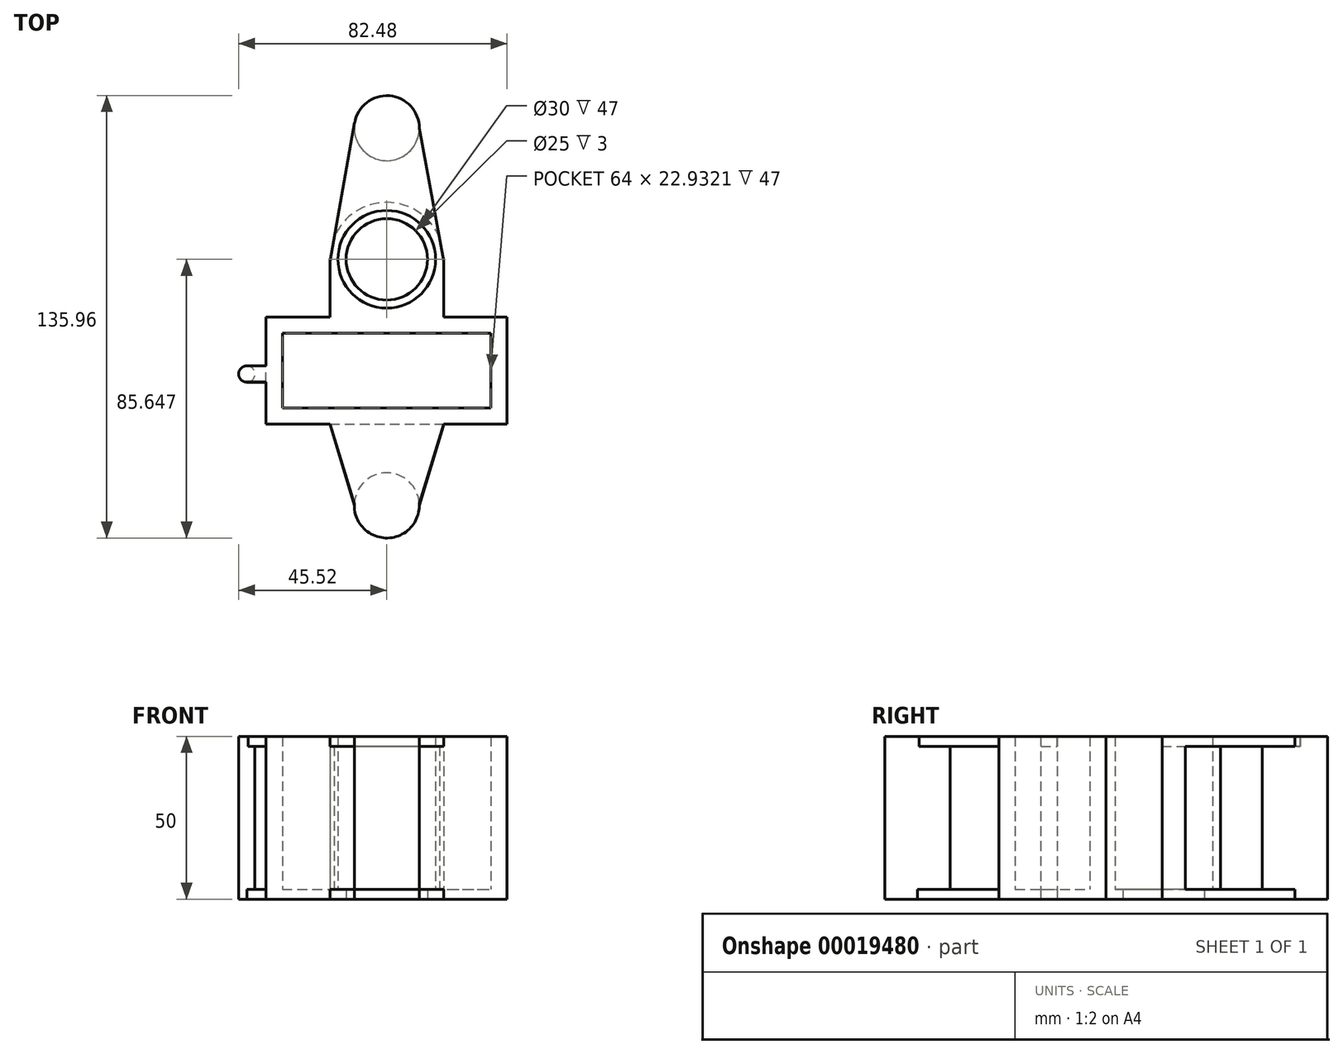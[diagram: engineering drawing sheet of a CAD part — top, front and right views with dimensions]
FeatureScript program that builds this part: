
annotation { "Feature Type Name" : "Feature", "Feature Type Description" : "" }
export const myFeature = defineFeature(function(context is Context, id is Id, definition is map)
    precondition{}
    {
        {
            var Q0;
            Q0=qCreatedBy(makeId("Top.planeOp"),FACE);
            var sketch = newSketch(context, id + "F0", { "sketchPlane" : qUnion([Q0])});
            skLineSegment(sketch, "E0.bottom", {"start": v(0, 0) * mm, "end": v(64, 0) * mm});
            skLineSegment(sketch, "E0.top", {"start": v(0, 22.93) * mm, "end": v(64, 22.93) * mm});
            skLineSegment(sketch, "E0.left", {"start": v(0, 0) * mm, "end": v(0, 22.93) * mm});
            skLineSegment(sketch, "E0.right", {"start": v(64, 0) * mm, "end": v(64, 22.93) * mm});
            skLineSegment(sketch, "E1.0", {"start": v(-5, 27.94) * mm, "end": v(14.57, 27.94) * mm});
            skLineSegment(sketch, "E1.1", {"start": v(-5, -5) * mm, "end": v(-5, 27.94) * mm});
            skLineSegment(sketch, "E1.2", {"start": v(-5, -5) * mm, "end": v(69, -5) * mm});
            skLineSegment(sketch, "E1.3", {"start": v(69, -5) * mm, "end": v(69, 27.94) * mm});
            skLineSegment(sketch, "E2", {"start": v(14.57, 45.02) * mm, "end": v(14.57, 27.94) * mm});
            skLineSegment(sketch, "E3", {"start": v(49.55, 45.16) * mm, "end": v(49.55, 27.94) * mm});
            skLineSegment(sketch, "E4.trimOffspring", {"start": v(49.55, 27.94) * mm, "end": v(69, 27.94) * mm});
            skCircle(sketch, "E5", {"center": v(32.06, 85.95) * mm, "radius": 10 * mm});
            skLineSegment(sketch, "E6", {"start": v(42.06, 85.95) * mm, "end": v(49.55, 45.16) * mm});
            skLineSegment(sketch, "E7", {"start": v(14.57, 45.02) * mm, "end": v(22.06, 85.95) * mm});
            skPoint(sketch, "E8.orphan", {"position": v(14.57, 85.95) * mm});
            skPoint(sketch, "E9.orphan", {"position": v(49.55, 85.95) * mm});
            skArc(sketch, "E10.trimOffspring", {"start": v(48.25, 52.25) * mm, "mid": v(32.14, 63.13) * mm, "end": v(15.92, 52.41) * mm});
            skCircle(sketch, "E11", {"center": v(-10.97, 10.38) * mm, "radius": 2.5 * mm});
            skLineSegment(sketch, "E12.top", {"start": v(-10.97, 7.83) * mm, "end": v(-5, 7.83) * mm});
            skLineSegment(sketch, "E12.left", {"start": v(-10.97, 7.88) * mm, "end": v(-10.97, 7.83) * mm});
            skLineSegment(sketch, "E12.right", {"start": v(-5, 10.38) * mm, "end": v(-5, 7.83) * mm});
            skLineSegment(sketch, "E13.top", {"start": v(-10.97, 12.92) * mm, "end": v(-5, 12.92) * mm});
            skLineSegment(sketch, "E13.left", {"start": v(-10.97, 12.88) * mm, "end": v(-10.97, 12.92) * mm});
            skLineSegment(sketch, "E13.right", {"start": v(-5, 10.38) * mm, "end": v(-5, 12.92) * mm});
            skCircle(sketch, "E14.0", {"center": v(32.05, 45.64) * mm, "radius": 12.5 * mm});
            skCircle(sketch, "E15.0", {"center": v(32.05, 45.64) * mm, "radius": 15 * mm});
            skCircle(sketch, "E16", {"center": v(32.05, -30) * mm, "radius": 10 * mm});
            skLineSegment(sketch, "E17", {"start": v(14.57, -5) * mm, "end": v(22.05, -30) * mm});
            skLineSegment(sketch, "E18", {"start": v(49.55, -5) * mm, "end": v(42.05, -30) * mm});
            skPoint(sketch, "E19.orphan", {"position": v(32.05, -5) * mm});
            skSolve(sketch);
        }
        {
            var Q0;
            Q0=makeQuery(id+"F0.imprint","IMPRINT",FACE,{"disambiguationData":[TD([[makeQuery(id+"F0.imprint","IMPRINT",EDGE,{"derivedFrom":sQuery(id+"F0.wireOp",EDGE,"E0.bottom")}),-1.0]])]});
            var Q1;
            {var subQ0=sQuery(id+"F0.wireOp",EDGE,"E5");var subQ2=makeQuery(id+"F0.imprint","INTERSECT",VERTEX,{"derivedFrom":[subQ0,sQuery(id+"F0.wireOp",EDGE,"E6")]});Q1=makeQuery(id+"F0.imprint","IMPRINT",FACE,{"disambiguationData":[TD([[makeQuery(id+"F0.imprint","IMPRINT",EDGE,{"disambiguationData":[TD([[subQ2,-1.0]])],"derivedFrom":subQ0}),1.0]])]});}
            var Q2;
            Q2=makeQuery(id+"F0.imprint","IMPRINT",FACE,{"disambiguationData":[TD([[makeQuery(id+"F0.imprint","IMPRINT",EDGE,{"derivedFrom":sQuery(id+"F0.wireOp",EDGE,"E11")}),1.0]])]});
            var Q3;
            {var subQ0=sQuery(id+"F0.wireOp",EDGE,"E16");var subQ2=makeQuery(id+"F0.imprint","INTERSECT",VERTEX,{"derivedFrom":[subQ0,sQuery(id+"F0.wireOp",EDGE,"E17")]});Q3=makeQuery(id+"F0.imprint","IMPRINT",FACE,{"disambiguationData":[TD([[makeQuery(id+"F0.imprint","IMPRINT",EDGE,{"disambiguationData":[TD([[subQ2,1.0]])],"derivedFrom":subQ0}),1.0]])]});}
            extrude(context, id + "F1", {"entities" : qUnion([Q0, Q1, Q2, Q3]), "depth" : 50 * mm});
        }
        {
            var Q0;
            Q0=makeQuery(id+"F0.imprint","IMPRINT",FACE,{"disambiguationData":[TD([[makeQuery(id+"F0.imprint","IMPRINT",EDGE,{"derivedFrom":sQuery(id+"F0.wireOp",EDGE,"E0.bottom")}),1.0]])]});
            var Q1;
            {var subQ0=sQuery(id+"F0.wireOp",EDGE,"E10.trimOffspring");Q1=makeQuery(id+"F0.imprint","IMPRINT",FACE,{"disambiguationData":[TD([[makeQuery(id+"F0.imprint","IMPRINT",EDGE,{"derivedFrom":subQ0}),-1.0]])]});}
            var Q2;
            Q2=makeQuery(id+"F0.imprint","IMPRINT",FACE,{"disambiguationData":[TD([[makeQuery(id+"F0.imprint","IMPRINT",EDGE,{"derivedFrom":sQuery(id+"F0.wireOp",EDGE,"E12.top")}),1.0]])]});
            var Q3;
            Q3=makeQuery(id+"F0.imprint","IMPRINT",FACE,{"disambiguationData":[TD([[makeQuery(id+"F0.imprint","IMPRINT",EDGE,{"derivedFrom":sQuery(id+"F0.wireOp",EDGE,"1a67a539-2671-4d19-8a7d-99683f66abed.0")}),-1.0]])]});
            var Q4;
            Q4=makeQuery(id+"F0.imprint","IMPRINT",FACE,{"disambiguationData":[TD([[makeQuery(id+"F0.imprint","IMPRINT",EDGE,{"derivedFrom":sQuery(id+"F0.wireOp",EDGE,"E14.0")}),-1.0]])]});
            var Q5;
            {var subQ1=sQuery(id+"F0.wireOp",EDGE,"E17");Q5=makeQuery(id+"F0.imprint","IMPRINT",FACE,{"disambiguationData":[TD([[makeQuery(id+"F0.imprint","IMPRINT",EDGE,{"derivedFrom":subQ1}),1.0]])]});}
            extrude(context, id + "F2", {"entities" : qUnion([Q0, Q1, Q2, Q3, Q4, Q5]), "operationType" : NewBodyOperationType.ADD, "depth" : 3 * mm});
        }
        {
            var Q0;
            Q0=makeQuery(id+"F1.opExtrude","CAP_FACE",FACE,{"disambiguationData":[OSD([sQuery(id+"F0.wireOp",EDGE,"E0.bottom"),sQuery(id+"F0.wireOp",EDGE,"E0.top"),sQuery(id+"F0.wireOp",EDGE,"E0.left"),sQuery(id+"F0.wireOp",EDGE,"E0.right"),sQuery(id+"F0.wireOp",EDGE,"E1.0"),sQuery(id+"F0.wireOp",EDGE,"E1.1"),sQuery(id+"F0.wireOp",EDGE,"E1.2"),sQuery(id+"F0.wireOp",EDGE,"E1.3"),sQuery(id+"F0.wireOp",EDGE,"1a67a539-2671-4d19-8a7d-99683f66abed.0"),sQuery(id+"F0.wireOp",EDGE,"E2"),sQuery(id+"F0.wireOp",EDGE,"E3"),sQuery(id+"F0.wireOp",EDGE,"E4.trimOffspring"),sQuery(id+"F0.wireOp",EDGE,"E6"),sQuery(id+"F0.wireOp",EDGE,"E7"),sQuery(id+"F0.wireOp",EDGE,"E10.trimOffspring")])],"isStart":false});
            var sketch = newSketch(context, id + "F3", { "sketchPlane" : qUnion([Q0])});
            skLineSegment(sketch, "E20", {"start": v(49.55, 45.16) * mm, "end": v(41.78, 87.45) * mm});
            skLineSegment(sketch, "E21", {"start": v(14.57, 45.02) * mm, "end": v(22.13, 87.52) * mm});
            skLineSegment(sketch, "E22", {"start": v(22.13, 87.52) * mm, "end": v(41.78, 87.45) * mm});
            skLineSegment(sketch, "E23.bottom", {"start": v(-10.79, 7.92) * mm, "end": v(-5, 7.92) * mm});
            skLineSegment(sketch, "E23.top", {"start": v(-10.79, 12.87) * mm, "end": v(-5, 12.87) * mm});
            skLineSegment(sketch, "E23.left", {"start": v(-10.79, 7.92) * mm, "end": v(-10.79, 12.87) * mm});
            skLineSegment(sketch, "E23.right", {"start": v(-5, 7.92) * mm, "end": v(-5, 12.87) * mm});
            skLineSegment(sketch, "E24", {"start": v(14.57, -5) * mm, "end": v(22.1, -29.68) * mm});
            skLineSegment(sketch, "E25", {"start": v(22.1, -29.68) * mm, "end": v(41.97, -29.68) * mm});
            skLineSegment(sketch, "E26", {"start": v(41.97, -29.68) * mm, "end": v(49.56, -5) * mm});
            skSolve(sketch);
        }
        {
            var Q0;
            Q0=makeQuery(id+"F3.imprint","IMPRINT",FACE,{"disambiguationData":[TD([[makeQuery(id+"F3.imprint","IMPRINT",EDGE,{"derivedFrom":sQuery(id+"F3.wireOp",EDGE,"E21")}),-1.0]])]});
            var Q1;
            Q1=makeQuery(id+"F3.imprint","IMPRINT",FACE,{"disambiguationData":[TD([[makeQuery(id+"F3.imprint","IMPRINT",EDGE,{"derivedFrom":sQuery(id+"F3.wireOp",EDGE,"E23.bottom")}),1.0]])]});
            var Q2;
            {var subQ2=sQuery(id+"F3.wireOp",EDGE,"E24");Q2=makeQuery(id+"F3.imprint","IMPRINT",FACE,{"disambiguationData":[TD([[makeQuery(id+"F3.imprint","IMPRINT",EDGE,{"derivedFrom":subQ2}),1.0]])]});}
            extrude(context, id + "F4", {"entities" : qUnion([Q0, Q1, Q2]), "operationType" : NewBodyOperationType.ADD, "oppositeDirection" : true, "depth" : 3 * mm});
        }
    });
